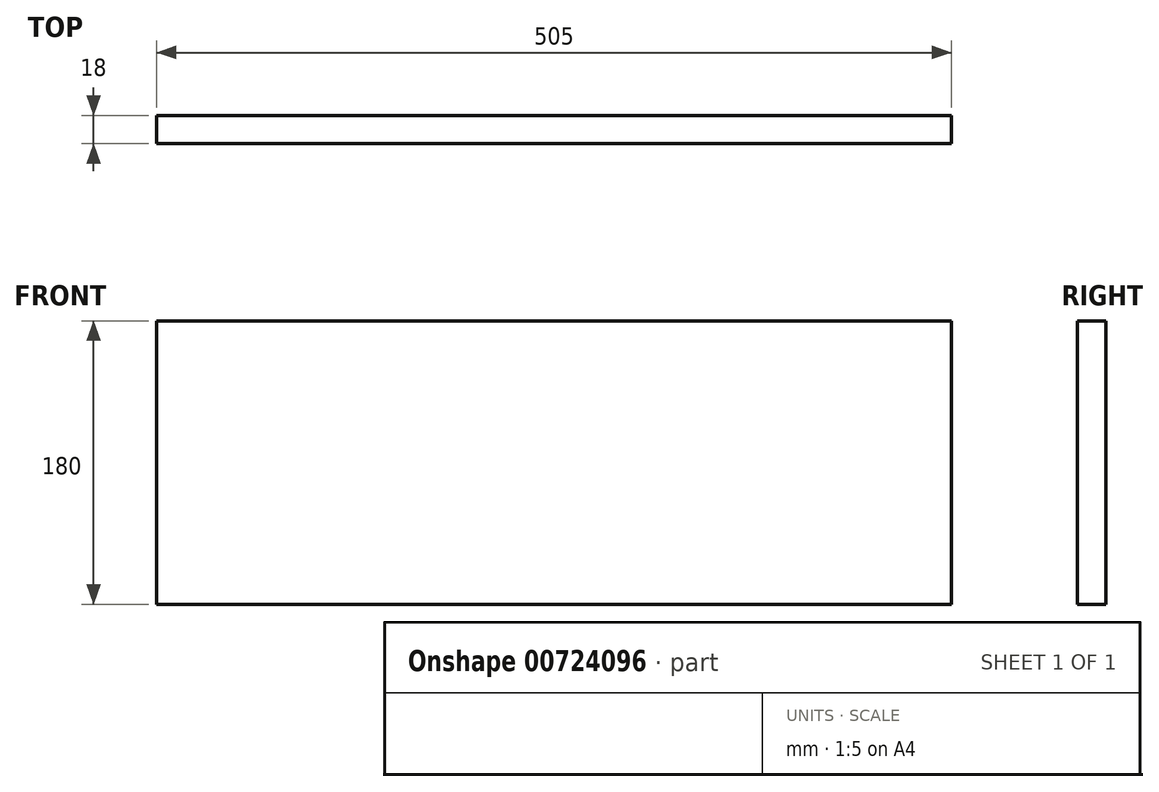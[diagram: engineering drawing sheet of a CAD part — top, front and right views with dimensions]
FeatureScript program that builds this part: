
annotation { "Feature Type Name" : "Feature", "Feature Type Description" : "" }
export const myFeature = defineFeature(function(context is Context, id is Id, definition is map)
    precondition{}
    {
        {
            var Q0;
            Q0=qCreatedBy(makeId("Front.planeOp"),FACE);
            var sketch = newSketch(context, id + "F0", { "sketchPlane" : qUnion([Q0])});
            skLineSegment(sketch, "E0.bottom", {"start": v(-252.5, 90) * mm, "end": v(252.5, 90) * mm});
            skLineSegment(sketch, "E0.top", {"start": v(-252.5, -90) * mm, "end": v(252.5, -90) * mm});
            skLineSegment(sketch, "E0.left", {"start": v(-252.5, 90) * mm, "end": v(-252.5, -90) * mm});
            skLineSegment(sketch, "E0.right", {"start": v(252.5, 90) * mm, "end": v(252.5, -90) * mm});
            skLineSegment(sketch, "E1", {"start": v(-252.5, 90) * mm, "end": v(252.5, -90) * mm, "construction": true});
            skSolve(sketch);
        }
        {
            var Q0;
            Q0=qSketchRegion(id+"F0",true);
            extrude(context, id + "F1", {"entities" : qUnion([Q0]), "depth" : 18 * mm, "offsetDistance" : 25 * mm});
        }
    });
